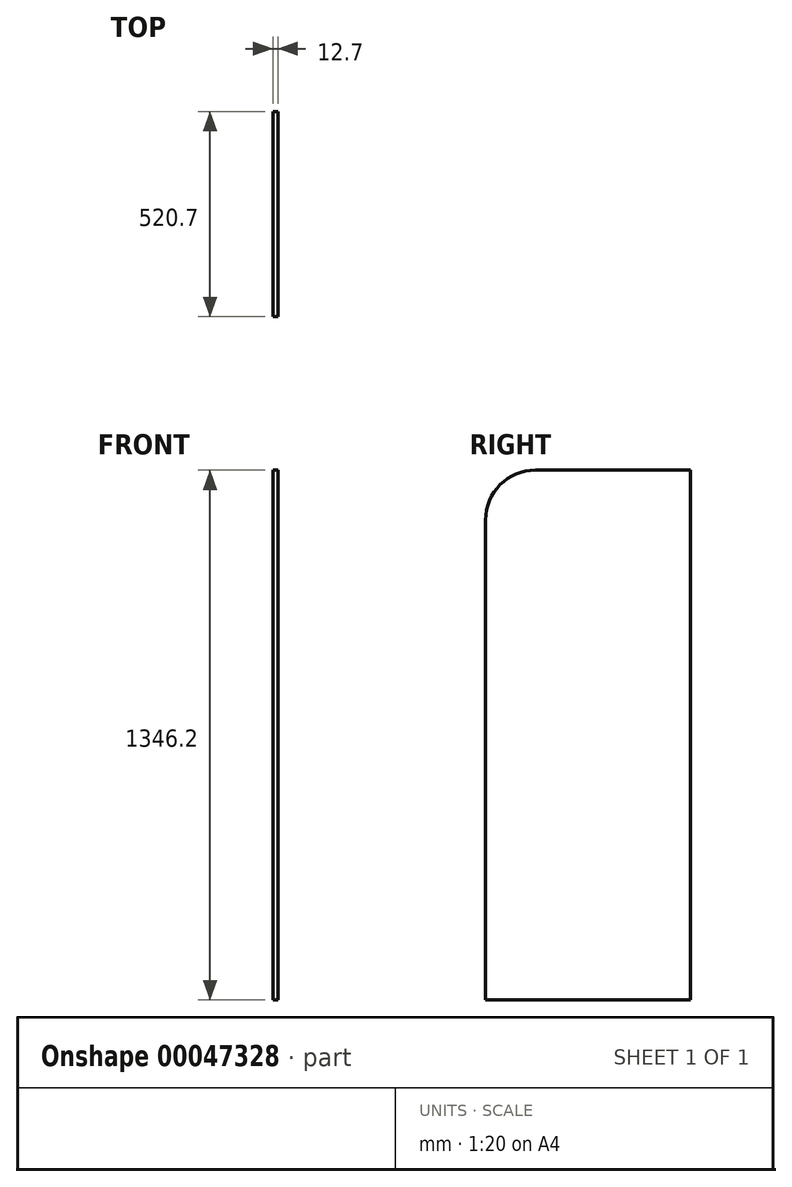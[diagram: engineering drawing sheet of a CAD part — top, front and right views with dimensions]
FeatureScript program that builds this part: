
annotation { "Feature Type Name" : "Feature", "Feature Type Description" : "" }
export const myFeature = defineFeature(function(context is Context, id is Id, definition is map)
    precondition{}
    {
        {
            var Q0;
            Q0=qCreatedBy(makeId("Right.planeOp"),FACE);
            var sketch = newSketch(context, id + "F0", { "sketchPlane" : qUnion([Q0])});
            skLineSegment(sketch, "E0.bottom", {"start": v(-30.78, 1274.48) * mm, "end": v(362.92, 1274.48) * mm});
            skLineSegment(sketch, "E0.top", {"start": v(-157.78, -71.72) * mm, "end": v(362.92, -71.72) * mm});
            skLineSegment(sketch, "E0.left", {"start": v(-157.78, 1147.48) * mm, "end": v(-157.78, -71.72) * mm});
            skLineSegment(sketch, "E0.right", {"start": v(362.92, 1274.48) * mm, "end": v(362.92, -71.72) * mm});
            skPoint(sketch, "E1.visualSharp", {"position": v(-157.78, 1274.48) * mm});
            skArc(sketch, "E1.filletArc", {"start": v(-30.78, 1274.48) * mm, "mid": v(-120.58, 1237.29) * mm, "end": v(-157.78, 1147.48) * mm});
            skSolve(sketch);
        }
        {
            var Q0;
            Q0=makeQuery(id+"F0.imprint","IMPRINT",FACE,{"disambiguationData":[TD([[makeQuery(id+"F0.imprint","IMPRINT",EDGE,{"derivedFrom":sQuery(id+"F0.wireOp",EDGE,"E0.bottom")}),-1.0]])]});
            extrude(context, id + "F1", {"entities" : qUnion([Q0]), "depth" : 12.7 * mm});
        }
    });
